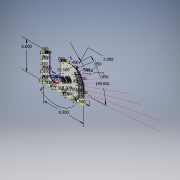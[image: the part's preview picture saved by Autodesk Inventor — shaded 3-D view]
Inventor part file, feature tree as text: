
AUTODESK INVENTOR PART (.ipt)
format: ipt  version: 2018 (Build 220112000, 112)  size: 280,576 bytes
history: native  units: in
note: dims shown in document units (in); Inventor stores cm internally (conversion verified against a paired STEP export)
features: sketch x2, extrude x2
ambient origin geometry x8: Origin, YZ Plane, XZ Plane, XY Plane, X Axis, Y Axis, Z Axis, Center Point
bodies: Solid1 (feature_tree)
feature tree (4):
  sketch  "Sketch1"  dims[d1=1.2in d2=8.5in]
  extrude  "Extrusion1"  Depth=8.5in
  sketch  "Sketch2"  dims[d3=6.0in d4=2.2in d5=0.0in d6=0.0344in d7=0.0687in d8=15.0deg d9=0.1374in d10=45.0deg d11=2.5in d12=0.1718in d13=0.2405in d14=30.0deg d15=0.2749in d16=45.0deg d19=0.95in d21=0.0in d22=10.5in d23=0.95in d26=0.95in d28=0.95in d30=0.95in d32=0.95in d34=0.95in d36=0.95in d38=0.95in d39=0.95in d41=8.0in d42=0.135in d43=0.135in d44=0.135in d45=0.135in d46=0.135in d47=0.135in d48=0.135in d49=0.135in d50=0.135in d51=0.135in d52=0.135in d53=0.135in d54=0.135in d55=0.135in d56=0.135in d57=0.135in d58=0.135in d59=0.135in d60=0.135in d61=0.135in d62=2.0in d63=0.1in d64=0.0in d65=0.15in d66=0.3in d67=1.0in d68=0.3in d69=1.0in d70=0.15in d71=0.3in d72=1.5in d73=0.3in d74=0.15in d75=1.5in d76=0.3in d77=0.15in d78=1.5in d79=0.3in d80=0.15in d81=2.3in d82=2.4in d83=0.3in d84=0.15in d85=0.05in d86=0.3in d87=0.15in d88=0.5in d89=0.15in d90=1.0in d91=0.0in]
  extrude  "Extrusion2"  Depth=2.2in
